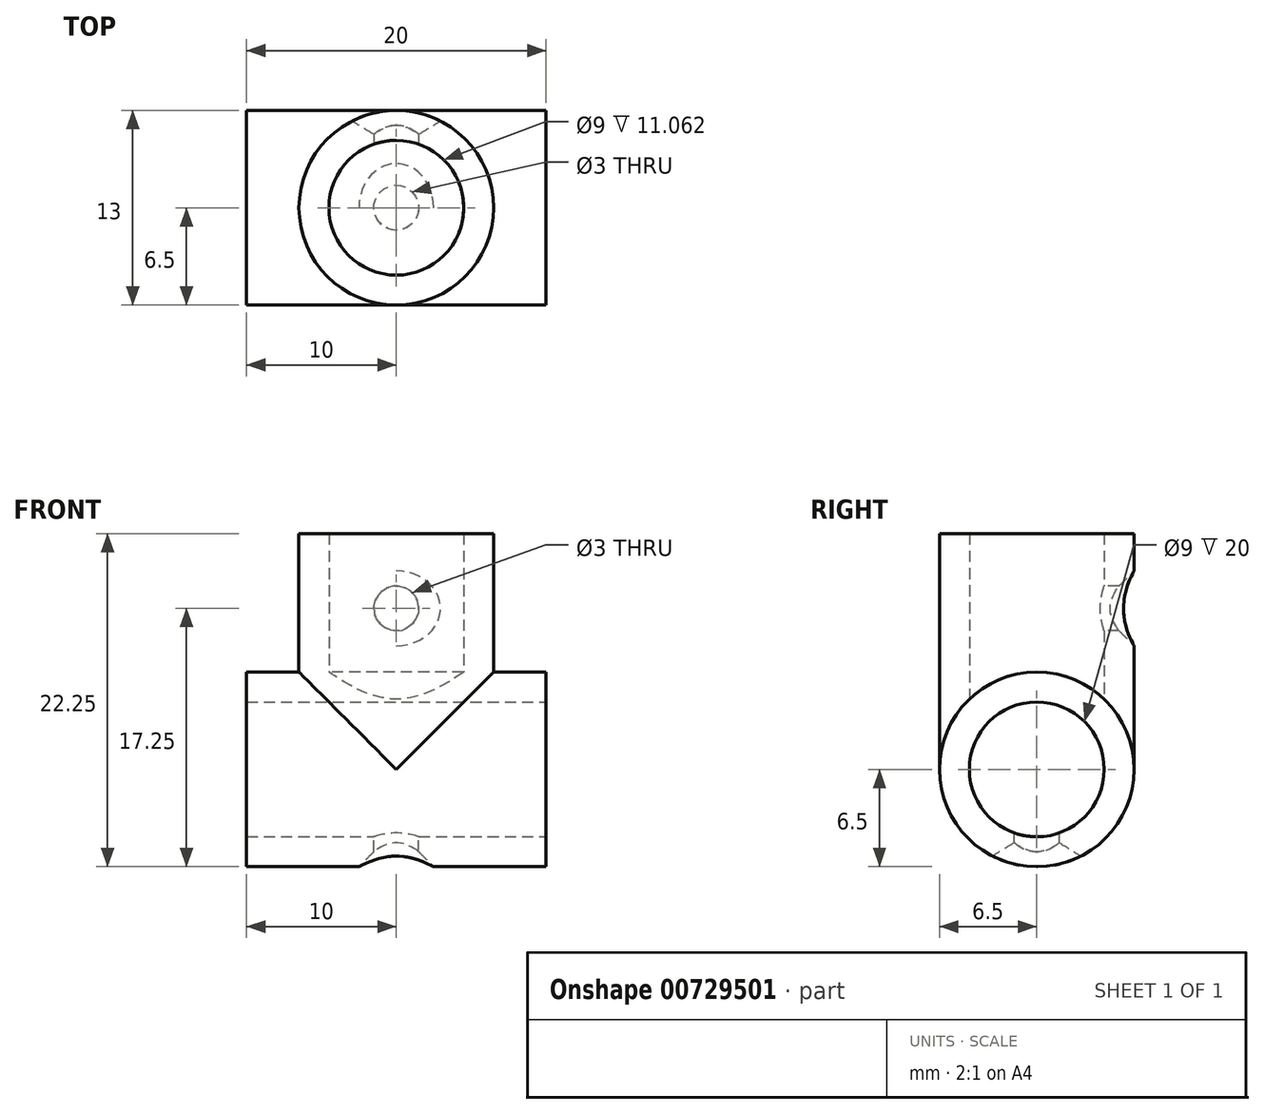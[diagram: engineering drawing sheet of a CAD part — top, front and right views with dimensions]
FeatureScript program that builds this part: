
annotation { "Feature Type Name" : "Feature", "Feature Type Description" : "" }
export const myFeature = defineFeature(function(context is Context, id is Id, definition is map)
    precondition{}
    {
        {
            var Q0;
            Q0=qCreatedBy(makeId("Right.planeOp"),FACE);
            var sketch = newSketch(context, id + "F0", { "sketchPlane" : qUnion([Q0])});
            skCircle(sketch, "E0", {"center": v(0, 0) * mm, "radius": 4.5 * mm});
            skCircle(sketch, "E1.0", {"center": v(0, 0) * mm, "radius": 6.5 * mm});
            skSolve(sketch);
        }
        {
            var Q0;
            Q0 = qSketchRegion(id + "F0", true);
            var Q1;
            Q1=makeQuery(id+"F0.imprint","IMPRINT",FACE,{"disambiguationData":[TD([[makeQuery(id+"F0.imprint","IMPRINT",EDGE,{"derivedFrom":sQuery(id+"F0.wireOp",EDGE,"E0")}),1.0]])]});
            extrude(context, id + "F1", {"entities" : qUnion([Q0, Q1]), "endBound" : BoundingType.SYMMETRIC, "depth" : 20 * mm, "offsetDistance" : 25 * mm});
        }
        {
            var Q0;
            Q0=qCreatedBy(makeId("Top.planeOp"),FACE);
            var sketch = newSketch(context, id + "F2", { "sketchPlane" : qUnion([Q0])});
            skCircle(sketch, "E2", {"center": v(0, 0) * mm, "radius": 6.5 * mm});
            skLineSegment(sketch, "E3", {"start": v(10, -6.5) * mm, "end": v(-10, -6.5) * mm, "construction": true});
            skCircle(sketch, "E4.0", {"center": v(0, 0) * mm, "radius": 4.5 * mm});
            skSolve(sketch);
        }
        {
            var Q0;
            Q0 = qSketchRegion(id + "F2", true);
            extrude(context, id + "F3", {"entities" : qUnion([Q0]), "operationType" : NewBodyOperationType.ADD, "depth" : (10 + (9.5 + 2) / 2) * mm, "offsetDistance" : 25 * mm});
        }
        {
            var Q0;
            Q0=makeQuery(id+"F0.imprint","IMPRINT",FACE,{"disambiguationData":[TD([[makeQuery(id+"F0.imprint","IMPRINT",EDGE,{"derivedFrom":sQuery(id+"F0.wireOp",EDGE,"E0")}),1.0]])]});
            extrude(context, id + "F4", {"entities" : qUnion([Q0]), "operationType" : NewBodyOperationType.REMOVE, "endBound" : BoundingType.SYMMETRIC, "oppositeDirection" : true, "depth" : 25 * mm, "offsetDistance" : 25 * mm});
        }
        {
            var Q0;
            Q0=qCreatedBy(makeId("Top.planeOp"),FACE);
            var sketch = newSketch(context, id + "F5", { "sketchPlane" : qUnion([Q0])});
            skCircle(sketch, "E5", {"center": v(0, 0) * mm, "radius": 1.5 * mm});
            skSolve(sketch);
        }
        {
            var Q0;
            Q0 = qSketchRegion(id + "F5", true);
            extrude(context, id + "F6", {"entities" : qUnion([Q0]), "operationType" : NewBodyOperationType.REMOVE, "oppositeDirection" : true, "depth" : 25 * mm, "offsetDistance" : 25 * mm});
        }
        {
            var Q0;
            Q0=qCreatedBy(makeId("Front.planeOp"),FACE);
            var sketch = newSketch(context, id + "F7", { "sketchPlane" : qUnion([Q0])});
            skCircle(sketch, "E6", {"center": v(0, 10.75) * mm, "radius": 1.5 * mm});
            skSolve(sketch);
        }
        {
            var Q0;
            Q0 = qSketchRegion(id + "F7", true);
            extrude(context, id + "F8", {"entities" : qUnion([Q0]), "operationType" : NewBodyOperationType.REMOVE, "oppositeDirection" : true, "depth" : 25 * mm, "offsetDistance" : 25 * mm});
        }
        {
            var Q0;
            {var subQ0=sQuery(id+"F0.wireOp",EDGE,"E1.0");Q0=makeQuery(id+"F6.boolean.opBoolean","INTERSECT",EDGE,{"derivedFrom":[makeQuery(id+"F3.boolean.opBoolean","SPLIT",FACE,{"disambiguationData":[TD([makeQuery(id+"F1.opExtrude","CAP_FACE",FACE,{"disambiguationData":[OSD([subQ0])],"isStart":true})])],"derivedFrom":makeQuery(id+"F1.opExtrude","SWEPT_FACE",FACE,{"disambiguationData":[OSD([subQ0])]})}),makeQuery(id+"F6.opExtrude","SWEPT_FACE",FACE,{"disambiguationData":[OSD([sQuery(id+"F5.wireOp",EDGE,"E5")])]})]});}
            var Q1;
            Q1=makeQuery(id+"F8.boolean.opBoolean","INTERSECT",EDGE,{"derivedFrom":[makeQuery(id+"F3.opExtrude","SWEPT_FACE",FACE,{"disambiguationData":[OSD([sQuery(id+"F2.wireOp",EDGE,"E2")])]}),makeQuery(id+"F8.opExtrude","SWEPT_FACE",FACE,{"disambiguationData":[OSD([sQuery(id+"F7.wireOp",EDGE,"E6")])]})]});
            chamfer(context, id + "F9", {"entities" : qUnion([Q0, Q1]), "chamferType" : ChamferType.OFFSET_ANGLE, "width" : 1 * mm, "oppositeDirection" : false, "angle" : 45 * degree, "tangentPropagation" : true});
        }
    });
